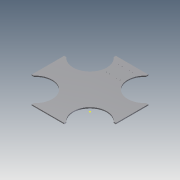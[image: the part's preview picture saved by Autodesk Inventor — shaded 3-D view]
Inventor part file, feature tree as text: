
AUTODESK INVENTOR PART (.ipt)
format: ipt  version: 2011 (Build 150239000, 239)  size: 780,288 bytes
history: native  units: in
note: dims shown in document units (in); Inventor stores cm internally (conversion verified against a paired STEP export)
features: sketch x24, extrude x23, fillet x4
ambient origin geometry x8: Origin, YZ Plane, XZ Plane, XY Plane, X Axis, Y Axis, Z Axis, Center Point
bodies: Solid1 (feature_tree)
feature tree (51):
  sketch  "Sketch1"  dims[d0=20.0in d1=20.0in d2=3.5in]
  extrude  "Extrusion1"  Depth=20.0in
  fillet  "Fillet1"  Radius=3.5in
  extrude  "Extrusion2"  Depth=3.5in
  extrude  "Extrusion3"  Depth=3.5in
  extrude  "Extrusion4"  Depth=3.5in
  extrude  "Extrusion5"  Depth=7.5in
  extrude  "Extrusion6"  Depth=7.5in
  extrude  "Extrusion7"  Depth=7.5in
  extrude  "Extrusion8"  Depth=0.5in TaperAngle=0.0deg
  extrude  "Extrusion9"  Depth=0.5in TaperAngle=0.0deg
  extrude  "Extrusion10"  Depth=4.5635in
  extrude  "Extrusion11"  Depth=2.6in
  fillet  "Fillet2"  Radius=2.6in
  fillet  "Fillet3"  Radius=5.2in
  fillet  "Fillet4"  Radius=5.2in
  extrude  "Extrusion12"  Depth=0.25in
  extrude  "Extrusion13"  Depth=0.25in
  extrude  "Extrusion14"  Depth=0.25in
  extrude  "Extrusion15"  Depth=0.25in
  extrude  "Extrusion16"  Depth=0.25in
  extrude  "Extrusion17"  Depth=0.25in
  extrude  "Extrusion18"  Depth=1.0in TaperAngle=0.0deg
  extrude  "Extrusion19"  Depth=1.5in
  extrude  "Extrusion20"  Depth=1.5in
  extrude  "Extrusion21"  Depth=0.25in
  extrude  "Extrusion22"  Depth=0.25in
  extrude  "Extrusion23"  Depth=0.25in
  sketch  "Sketch2"  dims[d3=3.5in d4=3.5in]
  sketch  "Sketch3"  dims[d5=3.5in d6=3.5in]
  sketch  "Sketch4"  dims[d7=3.5in d8=3.5in]
  sketch  "Sketch5"  dims[d9=3.5in d10=7.5in]
  sketch  "Sketch6"  dims[d11=7.5in d12=7.5in]
  sketch  "Sketch7"  dims[d13=7.5in d14=7.5in]
  sketch  "Sketch8"  dims[d15=7.5in d16=0.5in d17=0.0in]
  sketch  "Sketch9"  dims[d18=4.0in d19=0.5in d20=0.0in]
  sketch  "Sketch10"  dims[d21=0.5in d22=0.0in d23=4.5635in]
  sketch  "Sketch11"  dims[d24=4.5635in d25=2.6in d26=2.6in d27=5.2in d28=5.2in]
  sketch  "Sketch12"  dims[d29=0.25in d30=0.25in]
  sketch  "Sketch13"  dims[d31=0.25in d32=0.25in]
  sketch  "Sketch14"  dims[d33=0.25in d34=0.25in]
  sketch  "Sketch15"  dims[d35=5.2in d36=0.25in]
  sketch  "Sketch16"  dims[d37=0.25in d38=0.25in]
  sketch  "Sketch17"  dims[d39=0.25in d40=0.25in]
  sketch  "Sketch18"  dims[d41=0.25in d42=1.0in d43=0.0in]
  sketch  "Sketch19"  dims[d44=0.25in d45=0.0in d46=1.5in]
  sketch  "Sketch20"  dims[d47=1.5in d48=1.5in]
  sketch  "Sketch21"  dims[d49=1.5in d50=0.25in]
  sketch  "Sketch22"  dims[d51=0.25in d52=0.25in]
  sketch  "Sketch23"  dims[d53=0.25in d54=0.25in]
  sketch  "Sketch24"  dims[d55=0.25in d56=0.25in d57=0.25in d58=0.25in d59=0.25in d60=0.25in d61=0.25in d62=0.25in d63=0.0in d64=1.5in d65=1.5in d66=0.25in d67=0.5in d68=1.0in d69=0.25in d70=1.0in d71=1.0in d72=1.0in d73=0.5in d74=0.5in d75=1.0in d76=0.0in d77=0.25in d78=0.0in d79=4.5635in d80=0.6in d81=1.2in d82=0.5in d83=0.25in d84=0.5in d85=0.25in d86=1.0in d87=1.0in d88=1.0in d89=1.0in d90=0.25in d91=0.0in d92=0.25in d93=0.0in d94=1.0in d95=1.0in d96=0.25in d97=0.0in d98=0.125in d99=0.125in d100=0.125in d101=0.25in d102=0.25in d103=0.25in d104=0.25in d105=0.25in d106=0.25in d107=0.25in d108=0.25in d109=0.0in d110=0.25in d111=0.25in d112=0.25in d113=0.0in d114=0.25in d115=0.0in d116=2.85in d117=5.7in d118=0.75in d119=0.5in d120=0.75in d121=0.25in d122=0.0in d123=0.25in d124=0.0in d125=0.5in d126=0.25in d127=0.0in d128=0.5in d129=0.25in d130=0.0in d131=3.85in d132=7.7in d133=0.25in d134=0.0in d135=3.85in d136=7.7in d137=1.0in d138=0.0in d139=9.0in d140=7.7in d141=9.0in d142=0.5in d143=1.0in d144=0.5in d145=1.0in d146=1.0in d147=0.0in d148=0.25in d149=0.0in d150=1.25in d151=1.5in d152=3.0in d153=0.4in d154=0.8in d155=0.4in d156=0.8in d157=1.25in d158=1.5in d159=3.0in d160=0.4in d161=0.8in d162=0.4in d163=0.8in d164=0.14in d165=0.25in d166=0.0in]
